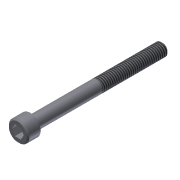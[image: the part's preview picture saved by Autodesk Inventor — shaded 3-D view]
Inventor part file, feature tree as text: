
AUTODESK INVENTOR PART (.ipt)
format: ipt  version: 2013 (Build 170138000, 138)  size: 99,840 bytes
history: native  units: in
note: dims shown in document units (in); Inventor stores cm internally (conversion verified against a paired STEP export)
features: extrude x3, sketch x3, chamfer x2, thread x1
ambient origin geometry x8: Origin, YZ Plane, XZ Plane, XY Plane, X Axis, Y Axis, Z Axis, Center Point
bodies: Solid1 (feature_tree)
feature tree (9):
  extrude  "Extrusion1"  Depth=0.19in TaperAngle=0.0deg
  extrude  "Extrusion2"  Depth=2.0in TaperAngle=0.0deg
  extrude  "Extrusion3"  Depth=0.125in TaperAngle=0.0deg
  thread  "Thread1"  [1 undecoded]
  chamfer  "Chamfer1"  Distance=0.02in Angle=45.0deg
  chamfer  "Chamfer2"  Distance=0.02in Angle=45.0deg
  sketch  "Sketch1"  dims[d0=0.312in d1=0.19in d2=0.0in]
  sketch  "Sketch2"  dims[d3=0.19in d4=2.0in d5=0.0in]
  sketch  "Sketch3"  dims[d6=0.1562in d7=0.125in d8=0.0in d9=1.0in d10=0.0in d11=0.02in d12=0.125in d13=45.0deg d14=0.02in d15=0.125in d16=45.0deg]
note: 1 required parameter value undecoded (feature->parameter linkage not recoverable at this tier; creation-order binding heuristic only, values carry confidence <= 0.55)
